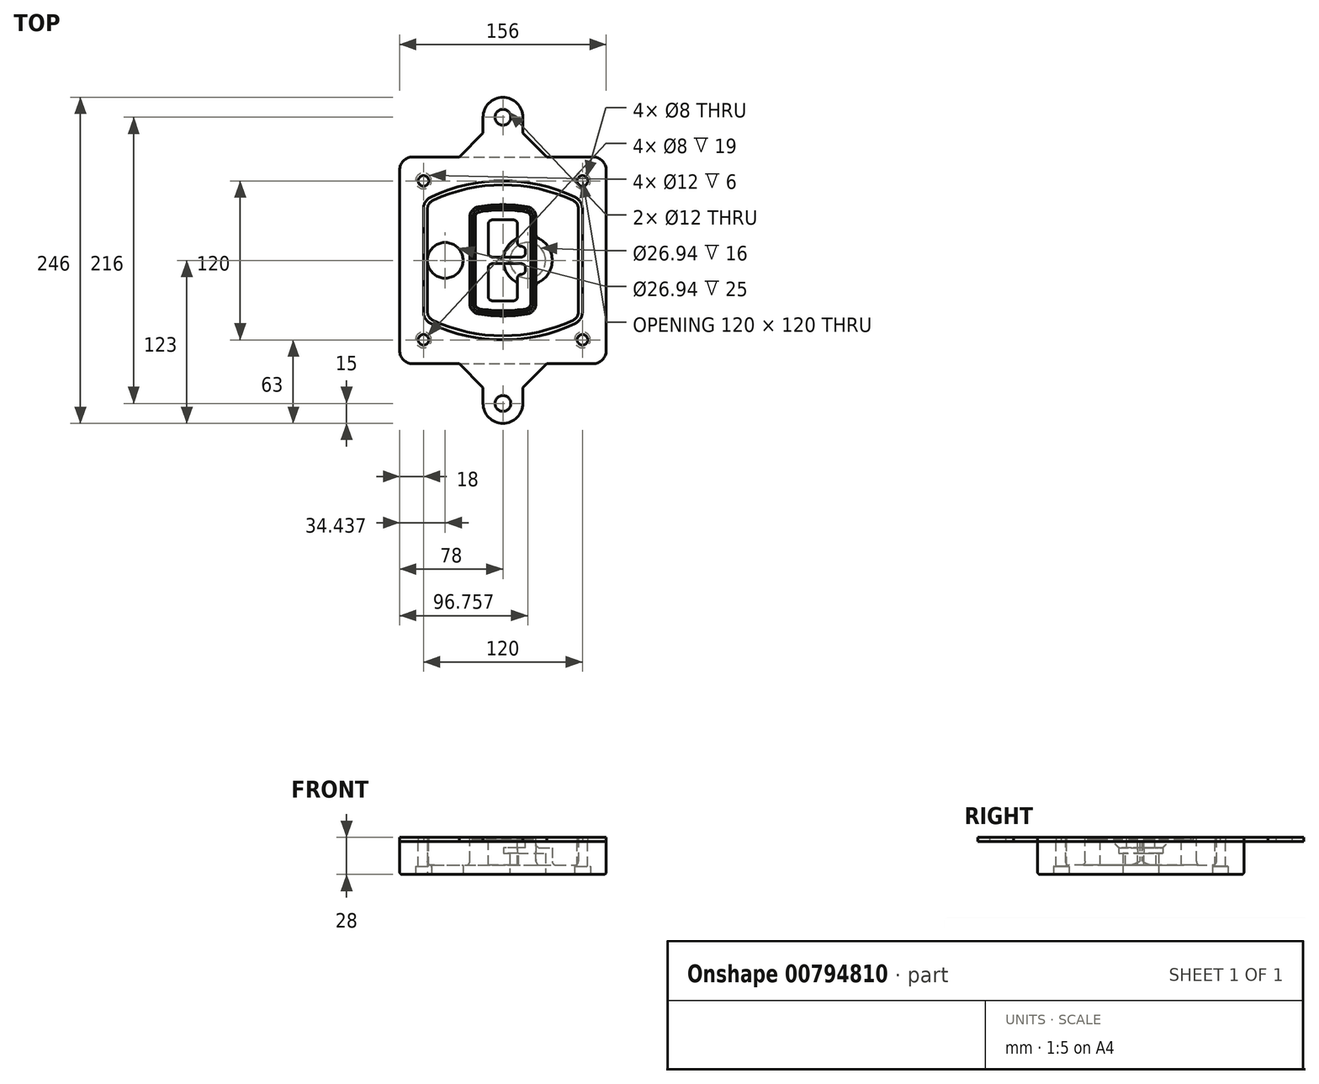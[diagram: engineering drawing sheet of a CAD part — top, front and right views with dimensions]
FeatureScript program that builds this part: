
annotation { "Feature Type Name" : "Feature", "Feature Type Description" : "" }
export const myFeature = defineFeature(function(context is Context, id is Id, definition is map)
    precondition{}
    {
        {
            var Q0;
            Q0=qCreatedBy(makeId("Top.planeOp"),FACE);
            var sketch = newSketch(context, id + "F0", { "sketchPlane" : qUnion([Q0])});
            skPoint(sketch, "E0.rect.middle", {"position": v(0, 0) * mm});
            skLineSegment(sketch, "E1.bottom", {"start": v(-68, -78) * mm, "end": v(68, -78) * mm});
            skLineSegment(sketch, "E1.top", {"start": v(-68, 78) * mm, "end": v(68, 78) * mm});
            skLineSegment(sketch, "E1.left", {"start": v(-78, -68) * mm, "end": v(-78, 68) * mm});
            skLineSegment(sketch, "E1.right", {"start": v(78, -68) * mm, "end": v(78, 68) * mm});
            skLineSegment(sketch, "E2", {"start": v(-78, 78) * mm, "end": v(78, -78) * mm, "construction": true});
            skLineSegment(sketch, "E3", {"start": v(78, 78) * mm, "end": v(-78, -78) * mm, "construction": true});
            skCircle(sketch, "E4", {"center": v(-60, 60) * mm, "radius": 4 * mm});
            skCircle(sketch, "E5", {"center": v(60, 60) * mm, "radius": 4 * mm});
            skCircle(sketch, "E6", {"center": v(60, -60) * mm, "radius": 4 * mm});
            skCircle(sketch, "E7", {"center": v(-60, -60) * mm, "radius": 4 * mm});
            skLineSegment(sketch, "E8", {"start": v(-60, 60) * mm, "end": v(60, 60) * mm, "construction": true});
            skLineSegment(sketch, "E9", {"start": v(60, 60) * mm, "end": v(60, -60) * mm, "construction": true});
            skLineSegment(sketch, "E10", {"start": v(60, -60) * mm, "end": v(-60, -60) * mm, "construction": true});
            skLineSegment(sketch, "E11", {"start": v(-60, -60) * mm, "end": v(-60, 60) * mm, "construction": true});
            skLineSegment(sketch, "E12", {"start": v(-60, 38.83) * mm, "end": v(-60, -38.83) * mm});
            skLineSegment(sketch, "E13", {"start": v(60, 38.83) * mm, "end": v(60, -38.83) * mm});
            skArc(sketch, "E14", {"start": v(54.26, 47.88) * mm, "mid": v(0, 60) * mm, "end": v(-54.26, 47.88) * mm});
            skArc(sketch, "E15", {"start": v(-54.26, -47.88) * mm, "mid": v(0, -60) * mm, "end": v(54.26, -47.88) * mm});
            skLineSegment(sketch, "E16", {"start": v(-60, 0) * mm, "end": v(60, 0) * mm, "construction": true});
            skPoint(sketch, "E17.visualSharp", {"position": v(-60, -45) * mm});
            skArc(sketch, "E17.filletArc", {"start": v(-60, -38.83) * mm, "mid": v(-58.44, -44.2) * mm, "end": v(-54.26, -47.88) * mm});
            skPoint(sketch, "E18.visualSharp", {"position": v(-60, 45) * mm});
            skArc(sketch, "E18.filletArc", {"start": v(-54.26, 47.88) * mm, "mid": v(-58.44, 44.2) * mm, "end": v(-60, 38.83) * mm});
            skPoint(sketch, "E19.visualSharp", {"position": v(60, 45) * mm});
            skArc(sketch, "E19.filletArc", {"start": v(60, 38.83) * mm, "mid": v(58.44, 44.2) * mm, "end": v(54.26, 47.88) * mm});
            skPoint(sketch, "E20.visualSharp", {"position": v(60, -45) * mm});
            skArc(sketch, "E20.filletArc", {"start": v(54.26, -47.88) * mm, "mid": v(58.44, -44.2) * mm, "end": v(60, -38.83) * mm});
            skPoint(sketch, "E21.visualSharp", {"position": v(-78, 78) * mm});
            skArc(sketch, "E21.filletArc", {"start": v(-68, 78) * mm, "mid": v(-75.07, 75.07) * mm, "end": v(-78, 68) * mm});
            skPoint(sketch, "E22.visualSharp", {"position": v(78, 78) * mm});
            skArc(sketch, "E22.filletArc", {"start": v(78, 68) * mm, "mid": v(75.07, 75.07) * mm, "end": v(68, 78) * mm});
            skPoint(sketch, "E23.visualSharp", {"position": v(78, -78) * mm});
            skArc(sketch, "E23.filletArc", {"start": v(68, -78) * mm, "mid": v(75.07, -75.07) * mm, "end": v(78, -68) * mm});
            skPoint(sketch, "E24.visualSharp", {"position": v(-78, -78) * mm});
            skArc(sketch, "E24.filletArc", {"start": v(-78, -68) * mm, "mid": v(-75.07, -75.07) * mm, "end": v(-68, -78) * mm});
            skArc(sketch, "E25.0", {"start": v(57, 38.83) * mm, "mid": v(55.9, 42.58) * mm, "end": v(52.98, 45.17) * mm});
            skLineSegment(sketch, "E25.1", {"start": v(57, 38.83) * mm, "end": v(57, -38.83) * mm});
            skArc(sketch, "E25.2", {"start": v(52.98, -45.17) * mm, "mid": v(55.9, -42.58) * mm, "end": v(57, -38.83) * mm});
            skArc(sketch, "E25.3", {"start": v(-52.98, -45.17) * mm, "mid": v(0, -57) * mm, "end": v(52.98, -45.17) * mm});
            skArc(sketch, "E25.4", {"start": v(-57, -38.83) * mm, "mid": v(-55.9, -42.58) * mm, "end": v(-52.98, -45.17) * mm});
            skArc(sketch, "E25.5", {"start": v(52.98, 45.17) * mm, "mid": v(0, 57) * mm, "end": v(-52.98, 45.17) * mm});
            skLineSegment(sketch, "E25.6", {"start": v(-57, 38.83) * mm, "end": v(-57, -38.83) * mm});
            skArc(sketch, "E25.7", {"start": v(-52.98, 45.17) * mm, "mid": v(-55.9, 42.58) * mm, "end": v(-57, 38.83) * mm});
            skArc(sketch, "E26.0", {"start": v(-55.96, 51.5) * mm, "mid": v(-61.82, 46.33) * mm, "end": v(-64, 38.83) * mm});
            skArc(sketch, "E26.1", {"start": v(55.96, 51.5) * mm, "mid": v(0, 64) * mm, "end": v(-55.96, 51.5) * mm});
            skArc(sketch, "E26.2", {"start": v(64, 38.83) * mm, "mid": v(61.82, 46.33) * mm, "end": v(55.96, 51.5) * mm});
            skLineSegment(sketch, "E26.3", {"start": v(64, 38.83) * mm, "end": v(64, -38.83) * mm});
            skArc(sketch, "E26.4", {"start": v(55.96, -51.5) * mm, "mid": v(61.82, -46.33) * mm, "end": v(64, -38.83) * mm});
            skLineSegment(sketch, "E26.5", {"start": v(-64, 38.83) * mm, "end": v(-64, -38.83) * mm});
            skArc(sketch, "E26.6", {"start": v(-55.96, -51.5) * mm, "mid": v(0, -64) * mm, "end": v(55.96, -51.5) * mm});
            skArc(sketch, "E26.7", {"start": v(-64, -38.83) * mm, "mid": v(-61.82, -46.33) * mm, "end": v(-55.96, -51.5) * mm});
            skSolve(sketch);
        }
        {
            var Q0;
            Q0=makeQuery(id+"F0.imprint","IMPRINT",FACE,{"disambiguationData":[TD([[makeQuery(id+"F0.imprint","IMPRINT",EDGE,{"derivedFrom":sQuery(id+"F0.wireOp",EDGE,"E1.bottom")}),1.0]])]});
            var Q1;
            Q1=makeQuery(id+"F0.imprint","IMPRINT",FACE,{"disambiguationData":[TD([[makeQuery(id+"F0.imprint","IMPRINT",EDGE,{"derivedFrom":sQuery(id+"F0.wireOp",EDGE,"E12")}),1.0]])]});
            var Q2;
            Q2=makeQuery(id+"F0.imprint","IMPRINT",FACE,{"disambiguationData":[TD([[makeQuery(id+"F0.imprint","IMPRINT",EDGE,{"derivedFrom":sQuery(id+"F0.wireOp",EDGE,"E25.0")}),1.0]])]});
            var Q3;
            Q3=makeQuery(id+"F0.imprint","IMPRINT",FACE,{"disambiguationData":[TD([[makeQuery(id+"F0.imprint","IMPRINT",EDGE,{"derivedFrom":sQuery(id+"F0.wireOp",EDGE,"E12")}),-1.0]])]});
            extrude(context, id + "F1", {"entities" : qUnion([Q0, Q1, Q2, Q3]), "oppositeDirection" : true, "depth" : 25 * mm});
        }
        {
            var Q0;
            Q0=makeQuery(id+"F0.imprint","IMPRINT",FACE,{"disambiguationData":[TD([[makeQuery(id+"F0.imprint","IMPRINT",EDGE,{"derivedFrom":sQuery(id+"F0.wireOp",EDGE,"E12")}),1.0]])]});
            extrude(context, id + "F2", {"entities" : qUnion([Q0]), "operationType" : NewBodyOperationType.ADD, "depth" : 3 * mm});
        }
        {
            var Q0;
            Q0=makeQuery(id+"F0.imprint","IMPRINT",FACE,{"disambiguationData":[TD([[makeQuery(id+"F0.imprint","IMPRINT",EDGE,{"derivedFrom":sQuery(id+"F0.wireOp",EDGE,"E25.0")}),1.0]])]});
            extrude(context, id + "F3", {"entities" : qUnion([Q0]), "operationType" : NewBodyOperationType.REMOVE, "oppositeDirection" : true, "depth" : 18 * mm});
        }
        {
            var Q0;
            Q0=makeQuery(id+"F2.opExtrude","CAP_FACE",FACE,{"disambiguationData":[OSD([sQuery(id+"F0.wireOp",EDGE,"E12"),sQuery(id+"F0.wireOp",EDGE,"E13"),sQuery(id+"F0.wireOp",EDGE,"E14"),sQuery(id+"F0.wireOp",EDGE,"E15"),sQuery(id+"F0.wireOp",EDGE,"E17.filletArc"),sQuery(id+"F0.wireOp",EDGE,"E18.filletArc"),sQuery(id+"F0.wireOp",EDGE,"E19.filletArc"),sQuery(id+"F0.wireOp",EDGE,"E20.filletArc"),sQuery(id+"F0.wireOp",EDGE,"E25.0"),sQuery(id+"F0.wireOp",EDGE,"E25.1"),sQuery(id+"F0.wireOp",EDGE,"E25.2"),sQuery(id+"F0.wireOp",EDGE,"E25.3"),sQuery(id+"F0.wireOp",EDGE,"E25.4"),sQuery(id+"F0.wireOp",EDGE,"E25.5"),sQuery(id+"F0.wireOp",EDGE,"E25.6"),sQuery(id+"F0.wireOp",EDGE,"E25.7")])],"isStart":false});
            var sketch = newSketch(context, id + "F4", { "sketchPlane" : qUnion([Q0])});
            skArc(sketch, "E27.0", {"start": v(-18.34, -40.45) * mm, "mid": v(0, -42) * mm, "end": v(18.34, -40.45) * mm});
            skArc(sketch, "E28.0", {"start": v(18.34, 40.45) * mm, "mid": v(0, 42) * mm, "end": v(-18.34, 40.45) * mm});
            skLineSegment(sketch, "E29", {"start": v(-25, 32.57) * mm, "end": v(-25, -32.57) * mm});
            skLineSegment(sketch, "E30", {"start": v(25, 32.57) * mm, "end": v(25, -32.57) * mm});
            skLineSegment(sketch, "E31", {"start": v(-25, 39.1) * mm, "end": v(25, 39.1) * mm, "construction": true});
            skLineSegment(sketch, "E32", {"start": v(-25, -39.1) * mm, "end": v(25, -39.1) * mm, "construction": true});
            skPoint(sketch, "E33.visualSharp", {"position": v(-25, 39.1) * mm});
            skArc(sketch, "E33.filletArc", {"start": v(-18.34, 40.45) * mm, "mid": v(-23.11, 37.73) * mm, "end": v(-25, 32.57) * mm});
            skPoint(sketch, "E34.visualSharp", {"position": v(25, 39.1) * mm});
            skArc(sketch, "E34.filletArc", {"start": v(25, 32.57) * mm, "mid": v(23.11, 37.73) * mm, "end": v(18.34, 40.45) * mm});
            skPoint(sketch, "E35.visualSharp", {"position": v(25, -39.1) * mm});
            skArc(sketch, "E35.filletArc", {"start": v(18.34, -40.45) * mm, "mid": v(23.11, -37.73) * mm, "end": v(25, -32.57) * mm});
            skPoint(sketch, "E36.visualSharp", {"position": v(-25, -39.1) * mm});
            skArc(sketch, "E36.filletArc", {"start": v(-25, -32.57) * mm, "mid": v(-23.11, -37.73) * mm, "end": v(-18.34, -40.45) * mm});
            skArc(sketch, "E37.0", {"start": v(52.98, 45.17) * mm, "mid": v(0, 57) * mm, "end": v(-52.98, 45.17) * mm});
            skArc(sketch, "E37.1", {"start": v(-52.98, 45.17) * mm, "mid": v(-55.9, 42.58) * mm, "end": v(-57, 38.83) * mm});
            skLineSegment(sketch, "E37.2", {"start": v(-57, 38.83) * mm, "end": v(-57, -38.83) * mm});
            skArc(sketch, "E37.3", {"start": v(-57, -38.83) * mm, "mid": v(-55.9, -42.58) * mm, "end": v(-52.98, -45.17) * mm});
            skArc(sketch, "E37.4", {"start": v(-52.98, -45.17) * mm, "mid": v(0, -57) * mm, "end": v(52.98, -45.17) * mm});
            skArc(sketch, "E37.5", {"start": v(52.98, -45.17) * mm, "mid": v(55.9, -42.58) * mm, "end": v(57, -38.83) * mm});
            skLineSegment(sketch, "E37.6", {"start": v(57, 38.83) * mm, "end": v(57, -38.83) * mm});
            skArc(sketch, "E37.7", {"start": v(57, 38.83) * mm, "mid": v(55.9, 42.58) * mm, "end": v(52.98, 45.17) * mm});
            skLineSegment(sketch, "E38.0", {"start": v(23, 32.57) * mm, "end": v(23, -32.57) * mm});
            skArc(sketch, "E38.1", {"start": v(18, -38.48) * mm, "mid": v(21.58, -36.44) * mm, "end": v(23, -32.57) * mm});
            skArc(sketch, "E38.2", {"start": v(-18, -38.48) * mm, "mid": v(0, -40) * mm, "end": v(18, -38.48) * mm});
            skArc(sketch, "E38.3", {"start": v(-23, -32.57) * mm, "mid": v(-21.58, -36.44) * mm, "end": v(-18, -38.48) * mm});
            skLineSegment(sketch, "E38.4", {"start": v(-23, 32.57) * mm, "end": v(-23, -32.57) * mm});
            skArc(sketch, "E38.5", {"start": v(23, 32.57) * mm, "mid": v(21.58, 36.44) * mm, "end": v(18, 38.48) * mm});
            skArc(sketch, "E38.6", {"start": v(-18, 38.48) * mm, "mid": v(-21.58, 36.44) * mm, "end": v(-23, 32.57) * mm});
            skArc(sketch, "E38.7", {"start": v(18, 38.48) * mm, "mid": v(0, 40) * mm, "end": v(-18, 38.48) * mm});
            skArc(sketch, "E39.0", {"start": v(21, 32.57) * mm, "mid": v(20.06, 35.15) * mm, "end": v(17.67, 36.5) * mm});
            skLineSegment(sketch, "E39.1", {"start": v(21, 32.57) * mm, "end": v(21, -32.57) * mm});
            skArc(sketch, "E39.2", {"start": v(17.67, -36.5) * mm, "mid": v(20.06, -35.15) * mm, "end": v(21, -32.57) * mm});
            skArc(sketch, "E39.3", {"start": v(-17.67, -36.5) * mm, "mid": v(0, -38) * mm, "end": v(17.67, -36.5) * mm});
            skArc(sketch, "E39.4", {"start": v(-21, -32.57) * mm, "mid": v(-20.06, -35.15) * mm, "end": v(-17.67, -36.5) * mm});
            skArc(sketch, "E39.5", {"start": v(17.67, 36.5) * mm, "mid": v(0, 38) * mm, "end": v(-17.67, 36.5) * mm});
            skLineSegment(sketch, "E39.6", {"start": v(-21, 32.57) * mm, "end": v(-21, -32.57) * mm});
            skArc(sketch, "E39.7", {"start": v(-17.67, 36.5) * mm, "mid": v(-20.06, 35.15) * mm, "end": v(-21, 32.57) * mm});
            skLineSegment(sketch, "E40", {"start": v(-25, 0) * mm, "end": v(25, 0) * mm, "construction": true});
            skLineSegment(sketch, "E41", {"start": v(-11, 5.5) * mm, "end": v(-11, 27.5) * mm});
            skLineSegment(sketch, "E42", {"start": v(-8, 30.5) * mm, "end": v(8, 30.5) * mm});
            skLineSegment(sketch, "E43", {"start": v(11, 27.5) * mm, "end": v(11, 13.5) * mm});
            skLineSegment(sketch, "E44", {"start": v(14, 10.5) * mm, "end": v(14, 10.5) * mm});
            skLineSegment(sketch, "E45", {"start": v(17, 7.5) * mm, "end": v(17, 5.5) * mm});
            skLineSegment(sketch, "E46", {"start": v(14, 2.5) * mm, "end": v(-8, 2.5) * mm});
            skPoint(sketch, "E47.visualSharp", {"position": v(-11, 30.5) * mm});
            skArc(sketch, "E47.filletArc", {"start": v(-8, 30.5) * mm, "mid": v(-10.12, 29.62) * mm, "end": v(-11, 27.5) * mm});
            skPoint(sketch, "E48.visualSharp", {"position": v(11, 30.5) * mm});
            skArc(sketch, "E48.filletArc", {"start": v(11, 27.5) * mm, "mid": v(10.12, 29.62) * mm, "end": v(8, 30.5) * mm});
            skPoint(sketch, "E49.visualSharp", {"position": v(11, 10.5) * mm});
            skArc(sketch, "E49.filletArc", {"start": v(11, 13.5) * mm, "mid": v(11.88, 11.38) * mm, "end": v(14, 10.5) * mm});
            skPoint(sketch, "E50.visualSharp", {"position": v(17, 10.5) * mm});
            skArc(sketch, "E50.filletArc", {"start": v(17, 7.5) * mm, "mid": v(16.12, 9.62) * mm, "end": v(14, 10.5) * mm});
            skPoint(sketch, "E51.visualSharp", {"position": v(17, 2.5) * mm});
            skArc(sketch, "E51.filletArc", {"start": v(14, 2.5) * mm, "mid": v(16.12, 3.38) * mm, "end": v(17, 5.5) * mm});
            skPoint(sketch, "E52.visualSharp", {"position": v(-11, 2.5) * mm});
            skArc(sketch, "E52.filletArc", {"start": v(-11, 5.5) * mm, "mid": v(-10.12, 3.38) * mm, "end": v(-8, 2.5) * mm});
            skLineSegment(sketch, "E53.0.MirrorCS", {"start": v(14, -2.5) * mm, "end": v(-8, -2.5) * mm});
            skArc(sketch, "E54.0.MirrorCS", {"start": v(-11, -5.5) * mm, "mid": v(-10.12, -3.38) * mm, "end": v(-8, -2.5) * mm});
            skLineSegment(sketch, "E55.0.MirrorCS", {"start": v(-11, -5.5) * mm, "end": v(-11, -27.5) * mm});
            skArc(sketch, "E56.0.MirrorCS", {"start": v(-8, -30.5) * mm, "mid": v(-10.12, -29.62) * mm, "end": v(-11, -27.5) * mm});
            skLineSegment(sketch, "E57.0.MirrorCS", {"start": v(-8, -30.5) * mm, "end": v(8, -30.5) * mm});
            skArc(sketch, "E58.0.MirrorCS", {"start": v(11, -27.5) * mm, "mid": v(10.12, -29.62) * mm, "end": v(8, -30.5) * mm});
            skLineSegment(sketch, "E59.0.MirrorCS", {"start": v(11, -27.5) * mm, "end": v(11, -13.5) * mm});
            skArc(sketch, "E60.0.MirrorCS", {"start": v(11, -13.5) * mm, "mid": v(11.88, -11.38) * mm, "end": v(14, -10.5) * mm});
            skArc(sketch, "E61.0.MirrorCS", {"start": v(17, -7.5) * mm, "mid": v(16.12, -9.62) * mm, "end": v(14, -10.5) * mm});
            skLineSegment(sketch, "E62.0.MirrorCS", {"start": v(17, -7.5) * mm, "end": v(17, -5.5) * mm});
            skArc(sketch, "E63.0.MirrorCS", {"start": v(14, -2.5) * mm, "mid": v(16.12, -3.38) * mm, "end": v(17, -5.5) * mm});
            skSolve(sketch);
        }
        {
            var Q0;
            Q0=makeQuery(id+"F4.imprint","IMPRINT",FACE,{"disambiguationData":[TD([[makeQuery(id+"F4.imprint","IMPRINT",EDGE,{"derivedFrom":sQuery(id+"F4.wireOp",EDGE,"E27.0")}),1.0]])]});
            var Q1;
            Q1=makeQuery(id+"F4.imprint","IMPRINT",FACE,{"disambiguationData":[TD([[makeQuery(id+"F4.imprint","IMPRINT",EDGE,{"derivedFrom":sQuery(id+"F4.wireOp",EDGE,"E38.0")}),-1.0]])]});
            var Q2;
            Q2=makeQuery(id+"F4.imprint","IMPRINT",FACE,{"disambiguationData":[TD([[makeQuery(id+"F4.imprint","IMPRINT",EDGE,{"derivedFrom":sQuery(id+"F4.wireOp",EDGE,"E39.0")}),1.0]])]});
            extrude(context, id + "F5", {"entities" : qUnion([Q0, Q1, Q2]), "operationType" : NewBodyOperationType.ADD, "endBound" : BoundingType.UP_TO_NEXT, "oppositeDirection" : true, "depth" : 25 * mm});
        }
        {
            var Q0;
            Q0=makeQuery(id+"F4.imprint","IMPRINT",FACE,{"disambiguationData":[TD([[makeQuery(id+"F4.imprint","IMPRINT",EDGE,{"derivedFrom":sQuery(id+"F4.wireOp",EDGE,"E38.0")}),-1.0]])]});
            extrude(context, id + "F6", {"entities" : qUnion([Q0]), "operationType" : NewBodyOperationType.REMOVE, "oppositeDirection" : true, "depth" : 2 * mm});
        }
        {
            var Q0;
            Q0=makeQuery(id+"F1.opExtrude","CAP_FACE",FACE,{"disambiguationData":[OSD([sQuery(id+"F0.wireOp",EDGE,"E1.bottom"),sQuery(id+"F0.wireOp",EDGE,"E1.top"),sQuery(id+"F0.wireOp",EDGE,"E1.left"),sQuery(id+"F0.wireOp",EDGE,"E1.right"),sQuery(id+"F0.wireOp",EDGE,"E4"),sQuery(id+"F0.wireOp",EDGE,"E5"),sQuery(id+"F0.wireOp",EDGE,"E6"),sQuery(id+"F0.wireOp",EDGE,"E7"),sQuery(id+"F0.wireOp",EDGE,"E21.filletArc"),sQuery(id+"F0.wireOp",EDGE,"E22.filletArc"),sQuery(id+"F0.wireOp",EDGE,"E23.filletArc"),sQuery(id+"F0.wireOp",EDGE,"E24.filletArc")])],"isStart":false});
            var sketch = newSketch(context, id + "F7", { "sketchPlane" : qUnion([Q0])});
            skCircle(sketch, "E64", {"center": v(18.76, 0) * mm, "radius": 13.47 * mm});
            skCircle(sketch, "E65", {"center": v(-43.56, 0) * mm, "radius": 13.47 * mm});
            skLineSegment(sketch, "E66", {"start": v(78, 0) * mm, "end": v(-78, 0) * mm});
            skCircle(sketch, "E67", {"center": v(18.76, 0) * mm, "radius": 18.47 * mm});
            skCircle(sketch, "E68", {"center": v(60, -60) * mm, "radius": 6 * mm});
            skCircle(sketch, "E69", {"center": v(-60, -60) * mm, "radius": 6 * mm});
            skCircle(sketch, "E70", {"center": v(-60, 60) * mm, "radius": 6 * mm});
            skCircle(sketch, "E71", {"center": v(60, 60) * mm, "radius": 6 * mm});
            skSolve(sketch);
        }
        {
            var Q0;
            {var subQ1=sQuery(id+"F7.wireOp",EDGE,"E66");var subQ4=sQuery(id+"F7.wireOp",EDGE,"E64");var subQ6=makeQuery(id+"F7.imprint","INTERSECT",VERTEX,{"disambiguationData":[OD(0.0)],"derivedFrom":[subQ4,subQ1]});Q0=makeQuery(id+"F7.imprint","IMPRINT",FACE,{"disambiguationData":[TD([[makeQuery(id+"F7.imprint","IMPRINT",EDGE,{"disambiguationData":[TD([[subQ6,-1.0]])],"derivedFrom":subQ4}),-1.0]])]});}
            var Q1;
            {var subQ0=sQuery(id+"F7.wireOp",EDGE,"E66");var subQ1=sQuery(id+"F7.wireOp",EDGE,"E64");var subQ3=makeQuery(id+"F7.imprint","INTERSECT",VERTEX,{"disambiguationData":[OD(0.0)],"derivedFrom":[subQ1,subQ0]});Q1=makeQuery(id+"F7.imprint","IMPRINT",FACE,{"disambiguationData":[TD([[makeQuery(id+"F7.imprint","IMPRINT",EDGE,{"disambiguationData":[TD([[subQ3,-1.0]])],"derivedFrom":subQ1}),1.0]])]});}
            var Q2;
            {var subQ0=sQuery(id+"F7.wireOp",EDGE,"E66");var subQ1=sQuery(id+"F7.wireOp",EDGE,"E64");var subQ3=makeQuery(id+"F7.imprint","INTERSECT",VERTEX,{"disambiguationData":[OD(0.0)],"derivedFrom":[subQ1,subQ0]});Q2=makeQuery(id+"F7.imprint","IMPRINT",FACE,{"disambiguationData":[TD([[makeQuery(id+"F7.imprint","IMPRINT",EDGE,{"disambiguationData":[TD([[subQ3,1.0]])],"derivedFrom":subQ1}),1.0]])]});}
            var Q3;
            {var subQ1=sQuery(id+"F7.wireOp",EDGE,"E66");var subQ4=sQuery(id+"F7.wireOp",EDGE,"E64");var subQ6=makeQuery(id+"F7.imprint","INTERSECT",VERTEX,{"disambiguationData":[OD(0.0)],"derivedFrom":[subQ4,subQ1]});Q3=makeQuery(id+"F7.imprint","IMPRINT",FACE,{"disambiguationData":[TD([[makeQuery(id+"F7.imprint","IMPRINT",EDGE,{"disambiguationData":[TD([[subQ6,1.0]])],"derivedFrom":subQ4}),-1.0]])]});}
            extrude(context, id + "F8", {"entities" : qUnion([Q0, Q1, Q2, Q3]), "operationType" : NewBodyOperationType.ADD, "oppositeDirection" : true, "depth" : 20 * mm});
        }
        {
            var Q0;
            {var subQ0=sQuery(id+"F7.wireOp",EDGE,"E66");var subQ1=sQuery(id+"F7.wireOp",EDGE,"E64");var subQ3=makeQuery(id+"F7.imprint","INTERSECT",VERTEX,{"disambiguationData":[OD(0.0)],"derivedFrom":[subQ1,subQ0]});Q0=makeQuery(id+"F7.imprint","IMPRINT",FACE,{"disambiguationData":[TD([[makeQuery(id+"F7.imprint","IMPRINT",EDGE,{"disambiguationData":[TD([[subQ3,-1.0]])],"derivedFrom":subQ1}),1.0]])]});}
            var Q1;
            {var subQ0=sQuery(id+"F7.wireOp",EDGE,"E66");var subQ1=sQuery(id+"F7.wireOp",EDGE,"E64");var subQ3=makeQuery(id+"F7.imprint","INTERSECT",VERTEX,{"disambiguationData":[OD(0.0)],"derivedFrom":[subQ1,subQ0]});Q1=makeQuery(id+"F7.imprint","IMPRINT",FACE,{"disambiguationData":[TD([[makeQuery(id+"F7.imprint","IMPRINT",EDGE,{"disambiguationData":[TD([[subQ3,1.0]])],"derivedFrom":subQ1}),1.0]])]});}
            extrude(context, id + "F9", {"entities" : qUnion([Q0, Q1]), "operationType" : NewBodyOperationType.REMOVE, "oppositeDirection" : true, "depth" : 16 * mm});
        }
        {
            var Q0;
            {var subQ0=sQuery(id+"F7.wireOp",EDGE,"E66");var subQ1=sQuery(id+"F7.wireOp",EDGE,"E65");var subQ3=makeQuery(id+"F7.imprint","INTERSECT",VERTEX,{"disambiguationData":[OD(0.0)],"derivedFrom":[subQ1,subQ0]});Q0=makeQuery(id+"F7.imprint","IMPRINT",FACE,{"disambiguationData":[TD([[makeQuery(id+"F7.imprint","IMPRINT",EDGE,{"disambiguationData":[TD([[subQ3,-1.0]])],"derivedFrom":subQ1}),1.0]])]});}
            var Q1;
            {var subQ0=sQuery(id+"F7.wireOp",EDGE,"E66");var subQ1=sQuery(id+"F7.wireOp",EDGE,"E65");var subQ3=makeQuery(id+"F7.imprint","INTERSECT",VERTEX,{"disambiguationData":[OD(0.0)],"derivedFrom":[subQ1,subQ0]});Q1=makeQuery(id+"F7.imprint","IMPRINT",FACE,{"disambiguationData":[TD([[makeQuery(id+"F7.imprint","IMPRINT",EDGE,{"disambiguationData":[TD([[subQ3,1.0]])],"derivedFrom":subQ1}),1.0]])]});}
            extrude(context, id + "F10", {"entities" : qUnion([Q0, Q1]), "operationType" : NewBodyOperationType.REMOVE, "oppositeDirection" : true, "depth" : 25 * mm});
        }
        {
            var Q0;
            Q0=makeQuery(id+"F7.imprint","IMPRINT",FACE,{"disambiguationData":[TD([[makeQuery(id+"F7.imprint","IMPRINT",EDGE,{"derivedFrom":sQuery(id+"F7.wireOp",EDGE,"E68")}),1.0]])]});
            var Q1;
            Q1=makeQuery(id+"F7.imprint","IMPRINT",FACE,{"disambiguationData":[TD([[makeQuery(id+"F7.imprint","IMPRINT",EDGE,{"derivedFrom":makeQuery(id+"F1.opExtrude","CAP_EDGE",EDGE,{"disambiguationData":[OSD([sQuery(id+"F0.wireOp",EDGE,"E5")])],"isStart":false})}),-1.0]])]});
            var Q2;
            Q2=makeQuery(id+"F7.imprint","IMPRINT",FACE,{"disambiguationData":[TD([[makeQuery(id+"F7.imprint","IMPRINT",EDGE,{"derivedFrom":sQuery(id+"F7.wireOp",EDGE,"E69")}),1.0]])]});
            var Q3;
            Q3=makeQuery(id+"F7.imprint","IMPRINT",FACE,{"disambiguationData":[TD([[makeQuery(id+"F7.imprint","IMPRINT",EDGE,{"derivedFrom":makeQuery(id+"F1.opExtrude","CAP_EDGE",EDGE,{"disambiguationData":[OSD([sQuery(id+"F0.wireOp",EDGE,"E4")])],"isStart":false})}),-1.0]])]});
            var Q4;
            Q4=makeQuery(id+"F7.imprint","IMPRINT",FACE,{"disambiguationData":[TD([[makeQuery(id+"F7.imprint","IMPRINT",EDGE,{"derivedFrom":sQuery(id+"F7.wireOp",EDGE,"E70")}),1.0]])]});
            var Q5;
            Q5=makeQuery(id+"F7.imprint","IMPRINT",FACE,{"disambiguationData":[TD([[makeQuery(id+"F7.imprint","IMPRINT",EDGE,{"derivedFrom":makeQuery(id+"F1.opExtrude","CAP_EDGE",EDGE,{"disambiguationData":[OSD([sQuery(id+"F0.wireOp",EDGE,"E7")])],"isStart":false})}),-1.0]])]});
            var Q6;
            Q6=makeQuery(id+"F7.imprint","IMPRINT",FACE,{"disambiguationData":[TD([[makeQuery(id+"F7.imprint","IMPRINT",EDGE,{"derivedFrom":sQuery(id+"F7.wireOp",EDGE,"E71")}),1.0]])]});
            var Q7;
            Q7=makeQuery(id+"F7.imprint","IMPRINT",FACE,{"disambiguationData":[TD([[makeQuery(id+"F7.imprint","IMPRINT",EDGE,{"derivedFrom":makeQuery(id+"F1.opExtrude","CAP_EDGE",EDGE,{"disambiguationData":[OSD([sQuery(id+"F0.wireOp",EDGE,"E6")])],"isStart":false})}),-1.0]])]});
            extrude(context, id + "F11", {"entities" : qUnion([Q0, Q1, Q2, Q3, Q4, Q5, Q6, Q7]), "operationType" : NewBodyOperationType.REMOVE, "oppositeDirection" : true, "depth" : 6 * mm});
        }
        {
            var Q0;
            Q0=makeQuery(id+"F9.boolean.opBoolean","COPY",FACE,{"derivedFrom":makeQuery(id+"F9.opExtrude","CAP_FACE",FACE,{"disambiguationData":[OSD([sQuery(id+"F7.wireOp",EDGE,"E64")])],"isStart":false})});
            var sketch = newSketch(context, id + "F12", { "sketchPlane" : qUnion([Q0])});
            skArc(sketch, "E72.0", {"start": v(11, 16.76) * mm, "mid": v(3.9, 10.98) * mm, "end": v(0.46, 2.5) * mm});
            skArc(sketch, "E72.1", {"start": v(0.46, -2.5) * mm, "mid": v(3.9, -10.98) * mm, "end": v(11, -16.76) * mm});
            skLineSegment(sketch, "E73", {"start": v(0.46, -2.5) * mm, "end": v(14, -2.5) * mm});
            skLineSegment(sketch, "E74.0", {"start": v(14, 2.5) * mm, "end": v(0.46, 2.5) * mm});
            skArc(sketch, "E74.1", {"start": v(14, 2.5) * mm, "mid": v(16.12, 3.38) * mm, "end": v(17, 5.5) * mm});
            skLineSegment(sketch, "E74.2", {"start": v(17, 7.5) * mm, "end": v(17, 5.5) * mm});
            skArc(sketch, "E74.3", {"start": v(17, 7.5) * mm, "mid": v(16.12, 9.62) * mm, "end": v(14, 10.5) * mm});
            skArc(sketch, "E74.4", {"start": v(11, 13.5) * mm, "mid": v(11.88, 11.38) * mm, "end": v(14, 10.5) * mm});
            skLineSegment(sketch, "E74.5", {"start": v(11, 16.76) * mm, "end": v(11, 13.5) * mm});
            skLineSegment(sketch, "E74.7", {"start": v(14, -2.5) * mm, "end": v(0.46, -2.5) * mm});
            skArc(sketch, "E74.8", {"start": v(14, -2.5) * mm, "mid": v(16.12, -3.38) * mm, "end": v(17, -5.5) * mm});
            skLineSegment(sketch, "E74.9", {"start": v(17, -7.5) * mm, "end": v(17, -5.5) * mm});
            skArc(sketch, "E74.10", {"start": v(17, -7.5) * mm, "mid": v(16.12, -9.62) * mm, "end": v(14, -10.5) * mm});
            skArc(sketch, "E74.11", {"start": v(11, -13.5) * mm, "mid": v(11.88, -11.38) * mm, "end": v(14, -10.5) * mm});
            skLineSegment(sketch, "E74.12", {"start": v(11, -16.76) * mm, "end": v(11, -13.5) * mm});
            skPoint(sketch, "E75.orphan", {"position": v(11, -27.5) * mm});
            skPoint(sketch, "E76.orphan", {"position": v(-8, -2.5) * mm});
            skPoint(sketch, "E77.orphan", {"position": v(-8, 2.5) * mm});
            skPoint(sketch, "E78.orphan", {"position": v(11, 27.5) * mm});
            skSolve(sketch);
        }
        {
            var Q0;
            {var subQ7=sQuery(id+"F12.wireOp",EDGE,"E72.0");var subQ14=sQuery(id+"F12.wireOp",EDGE,"E72.1");var subQ16=sQuery(id+"F12.wireOp",EDGE,"E74.1");var subQ18=sQuery(id+"F12.wireOp",EDGE,"E74.8");Q0=qUnion([makeQuery(id+"F12.imprint","IMPRINT",FACE,{"disambiguationData":[TD([[makeQuery(id+"F12.imprint","IMPRINT",EDGE,{"derivedFrom":subQ7}),1.0]])]}),makeQuery(id+"F12.imprint","IMPRINT",FACE,{"disambiguationData":[TD([[makeQuery(id+"F12.imprint","IMPRINT",EDGE,{"derivedFrom":subQ14}),1.0]])]}),makeQuery(id+"F12.imprint","IMPRINT",FACE,{"disambiguationData":[TD([[makeQuery(id+"F12.imprint","IMPRINT",EDGE,{"derivedFrom":subQ16}),1.0]])]}),makeQuery(id+"F12.imprint","IMPRINT",FACE,{"disambiguationData":[TD([[makeQuery(id+"F12.imprint","IMPRINT",EDGE,{"derivedFrom":subQ18}),-1.0]])]})]);}
            var Q1;
            Q1=makeQuery(id+"F5.boolean.opBoolean","SPLIT",FACE,{"disambiguationData":[TD([makeQuery(id+"F5.opExtrude","SWEPT_FACE",FACE,{"disambiguationData":[OSD([sQuery(id+"F4.wireOp",EDGE,"E41")])]})])],"derivedFrom":makeQuery(id+"F3.boolean.opBoolean","COPY",FACE,{"derivedFrom":makeQuery(id+"F3.opExtrude","CAP_FACE",FACE,{"disambiguationData":[OSD([sQuery(id+"F0.wireOp",EDGE,"E25.0"),sQuery(id+"F0.wireOp",EDGE,"E25.1"),sQuery(id+"F0.wireOp",EDGE,"E25.2"),sQuery(id+"F0.wireOp",EDGE,"E25.3"),sQuery(id+"F0.wireOp",EDGE,"E25.4"),sQuery(id+"F0.wireOp",EDGE,"E25.5"),sQuery(id+"F0.wireOp",EDGE,"E25.6"),sQuery(id+"F0.wireOp",EDGE,"E25.7")])],"isStart":false})})});
            extrude(context, id + "F13", {"entities" : qUnion([Q0]), "operationType" : NewBodyOperationType.REMOVE, "endBound" : BoundingType.UP_TO_SURFACE, "endBoundEntityFace" : qUnion([Q1]), "depth" : 25 * mm});
        }
        {
            var Q0;
            Q0=makeQuery(id+"F3.boolean.opBoolean","COPY",EDGE,{"derivedFrom":makeQuery(id+"F3.opExtrude","CAP_EDGE",EDGE,{"disambiguationData":[OSD([sQuery(id+"F0.wireOp",EDGE,"E25.6")])],"isStart":false})});
            var Q1;
            Q1=makeQuery(id+"F8.boolean.opBoolean","INTERSECT",EDGE,{"derivedFrom":[makeQuery(id+"F5.opExtrude","SWEPT_FACE",FACE,{"disambiguationData":[OSD([sQuery(id+"F4.wireOp",EDGE,"E30")])]}),makeQuery(id+"F8.opExtrude","CAP_FACE",FACE,{"disambiguationData":[OSD([sQuery(id+"F7.wireOp",EDGE,"E67")])],"isStart":false})]});
            var Q2;
            Q2=makeQuery(id+"F8.boolean.opBoolean","INTERSECT",EDGE,{"disambiguationData":[OD(1.0)],"derivedFrom":[makeQuery(id+"F5.opExtrude","SWEPT_FACE",FACE,{"disambiguationData":[OSD([sQuery(id+"F4.wireOp",EDGE,"E30")])]}),makeQuery(id+"F8.opExtrude","SWEPT_FACE",FACE,{"disambiguationData":[OSD([sQuery(id+"F7.wireOp",EDGE,"E67")])]})]});
            var Q3;
            {var subQ0=sQuery(id+"F4.wireOp",EDGE,"E30");Q3=makeQuery(id+"F8.boolean.opBoolean","SPLIT",EDGE,{"disambiguationData":[TD([makeQuery(id+"F5.opExtrude","SWEPT_FACE",FACE,{"disambiguationData":[OSD([sQuery(id+"F4.wireOp",EDGE,"E35.filletArc")])]})])],"derivedFrom":makeQuery(id+"F5.opExtrude","CAP_EDGE",EDGE,{"disambiguationData":[OSD([subQ0])],"isStart":false})});}
            var Q4;
            {var subQ0=sQuery(id+"F0.wireOp",EDGE,"E25.7");var subQ1=sQuery(id+"F0.wireOp",EDGE,"E25.1");var subQ2=sQuery(id+"F0.wireOp",EDGE,"E25.6");var subQ3=sQuery(id+"F0.wireOp",EDGE,"E25.5");var subQ4=sQuery(id+"F0.wireOp",EDGE,"E25.4");var subQ5=sQuery(id+"F0.wireOp",EDGE,"E25.0");var subQ6=sQuery(id+"F0.wireOp",EDGE,"E25.2");var subQ7=sQuery(id+"F0.wireOp",EDGE,"E25.3");Q4=makeQuery(id+"F8.boolean.opBoolean","INTERSECT",EDGE,{"derivedFrom":[makeQuery(id+"F5.boolean.opBoolean","SPLIT",FACE,{"disambiguationData":[TD([makeQuery(id+"F2.opExtrude","SWEPT_FACE",FACE,{"disambiguationData":[OSD([subQ5])]})])],"derivedFrom":makeQuery(id+"F3.boolean.opBoolean","COPY",FACE,{"derivedFrom":makeQuery(id+"F3.opExtrude","CAP_FACE",FACE,{"disambiguationData":[OSD([subQ5,subQ1,subQ6,subQ7,subQ4,subQ3,subQ2,subQ0])],"isStart":false})})}),makeQuery(id+"F8.opExtrude","SWEPT_FACE",FACE,{"disambiguationData":[OSD([sQuery(id+"F7.wireOp",EDGE,"E67")])]})]});}
            var Q5;
            Q5=makeQuery(id+"F8.boolean.opBoolean","INTERSECT",EDGE,{"disambiguationData":[OD(0.0)],"derivedFrom":[makeQuery(id+"F5.opExtrude","SWEPT_FACE",FACE,{"disambiguationData":[OSD([sQuery(id+"F4.wireOp",EDGE,"E30")])]}),makeQuery(id+"F8.opExtrude","SWEPT_FACE",FACE,{"disambiguationData":[OSD([sQuery(id+"F7.wireOp",EDGE,"E67")])]})]});
            fillet(context, id + "F14", {"entities" : qUnion([Q0, Q1, Q2, Q3, Q4, Q5]), "radius" : 3 * mm, "tangentPropagation" : true, "allowEdgeOverflow" : false});
        }
        {
            var Q0;
            Q0=makeQuery(id+"F1.opExtrude","CAP_EDGE",EDGE,{"disambiguationData":[OSD([sQuery(id+"F0.wireOp",EDGE,"E1.bottom")])],"isStart":false});
            fillet(context, id + "F15", {"entities" : qUnion([Q0]), "radius" : 2 * mm, "tangentPropagation" : true, "allowEdgeOverflow" : false});
        }
        {
            var Q0;
            {var subQ0=sQuery(id+"F0.wireOp",EDGE,"E21.filletArc");var subQ1=sQuery(id+"F0.wireOp",EDGE,"E7");var subQ2=sQuery(id+"F0.wireOp",EDGE,"E6");var subQ3=sQuery(id+"F0.wireOp",EDGE,"E5");var subQ4=sQuery(id+"F0.wireOp",EDGE,"E4");var subQ5=sQuery(id+"F0.wireOp",EDGE,"E22.filletArc");var subQ6=sQuery(id+"F0.wireOp",EDGE,"E1.bottom");var subQ7=sQuery(id+"F0.wireOp",EDGE,"E1.right");var subQ8=sQuery(id+"F0.wireOp",EDGE,"E1.top");var subQ9=sQuery(id+"F0.wireOp",EDGE,"E1.left");var subQ10=sQuery(id+"F0.wireOp",EDGE,"E23.filletArc");var subQ11=sQuery(id+"F0.wireOp",EDGE,"E24.filletArc");Q0=makeQuery(id+"F2.boolean.opBoolean","SPLIT",FACE,{"disambiguationData":[TD([makeQuery(id+"F1.opExtrude","SWEPT_FACE",FACE,{"disambiguationData":[OSD([subQ6])]})])],"derivedFrom":makeQuery(id+"F1.opExtrude","CAP_FACE",FACE,{"disambiguationData":[OSD([subQ6,subQ8,subQ9,subQ7,subQ4,subQ3,subQ2,subQ1,subQ0,subQ5,subQ10,subQ11])],"isStart":true})});}
            var sketch = newSketch(context, id + "F16", { "sketchPlane" : qUnion([Q0])});
            skLineSegment(sketch, "E79.0", {"start": v(-78, -68) * mm, "end": v(-78, 68) * mm});
            skArc(sketch, "E79.1", {"start": v(-68, 78) * mm, "mid": v(-75.07, 75.07) * mm, "end": v(-78, 68) * mm});
            skLineSegment(sketch, "E79.2", {"start": v(-68, 78) * mm, "end": v(68, 78) * mm});
            skArc(sketch, "E79.3", {"start": v(78, 68) * mm, "mid": v(75.07, 75.07) * mm, "end": v(68, 78) * mm});
            skLineSegment(sketch, "E79.4", {"start": v(78, -68) * mm, "end": v(78, 68) * mm});
            skArc(sketch, "E79.5", {"start": v(68, -78) * mm, "mid": v(75.07, -75.07) * mm, "end": v(78, -68) * mm});
            skLineSegment(sketch, "E79.6", {"start": v(-68, -78) * mm, "end": v(68, -78) * mm});
            skArc(sketch, "E79.7", {"start": v(-78, -68) * mm, "mid": v(-75.07, -75.07) * mm, "end": v(-68, -78) * mm});
            skCircle(sketch, "E79.8", {"center": v(-60, -60) * mm, "radius": 4 * mm});
            skCircle(sketch, "E79.9", {"center": v(60, -60) * mm, "radius": 4 * mm});
            skCircle(sketch, "E79.10", {"center": v(60, 60) * mm, "radius": 4 * mm});
            skCircle(sketch, "E79.11", {"center": v(-60, 60) * mm, "radius": 4 * mm});
            skArc(sketch, "E79.12", {"start": v(-54.26, -47.88) * mm, "mid": v(0, -60) * mm, "end": v(54.26, -47.88) * mm});
            skLineSegment(sketch, "E79.13", {"start": v(60, 38.83) * mm, "end": v(60, -38.83) * mm});
            skArc(sketch, "E79.14", {"start": v(54.26, 47.88) * mm, "mid": v(0, 60) * mm, "end": v(-54.26, 47.88) * mm});
            skLineSegment(sketch, "E79.15", {"start": v(-60, 38.83) * mm, "end": v(-60, -38.83) * mm});
            skArc(sketch, "E79.16", {"start": v(-54.26, 47.88) * mm, "mid": v(-58.44, 44.2) * mm, "end": v(-60, 38.83) * mm});
            skArc(sketch, "E79.17", {"start": v(-60, -38.83) * mm, "mid": v(-58.44, -44.2) * mm, "end": v(-54.26, -47.88) * mm});
            skArc(sketch, "E79.18", {"start": v(60, 38.83) * mm, "mid": v(58.44, 44.2) * mm, "end": v(54.26, 47.88) * mm});
            skArc(sketch, "E79.19", {"start": v(54.26, -47.88) * mm, "mid": v(58.44, -44.2) * mm, "end": v(60, -38.83) * mm});
            skLineSegment(sketch, "E80", {"start": v(0, 78) * mm, "end": v(0, 108) * mm, "construction": true});
            skLineSegment(sketch, "E81", {"start": v(-15, 108) * mm, "end": v(-15, 96) * mm});
            skLineSegment(sketch, "E82", {"start": v(15, 96) * mm, "end": v(15, 108) * mm});
            skArc(sketch, "E83", {"start": v(15, 108) * mm, "mid": v(0, 123) * mm, "end": v(-15, 108) * mm});
            skLineSegment(sketch, "E84", {"start": v(-33, 78) * mm, "end": v(-15, 96) * mm});
            skLineSegment(sketch, "E85", {"start": v(33, 78) * mm, "end": v(15, 96) * mm});
            skCircle(sketch, "E86", {"center": v(0, 108) * mm, "radius": 6 * mm});
            skLineSegment(sketch, "E87", {"start": v(-78, 0) * mm, "end": v(78, 0) * mm, "construction": true});
            skArc(sketch, "E88.MirrorCS", {"start": v(-54.26, -47.88) * mm, "mid": v(-58.44, -44.2) * mm, "end": v(-60, -38.83) * mm});
            skLineSegment(sketch, "E89.MirrorCS", {"start": v(0, -78) * mm, "end": v(0, -108) * mm, "construction": true});
            skArc(sketch, "E90.MirrorCS", {"start": v(-68, -78) * mm, "mid": v(-75.07, -75.07) * mm, "end": v(-78, -68) * mm});
            skLineSegment(sketch, "E91.MirrorCS", {"start": v(-33, -78) * mm, "end": v(-15, -96) * mm});
            skCircle(sketch, "E92.MirrorC", {"center": v(0, -108) * mm, "radius": 6 * mm});
            skLineSegment(sketch, "E93.MirrorCS", {"start": v(-15, -108) * mm, "end": v(-15, -96) * mm});
            skArc(sketch, "E94.MirrorCS", {"start": v(54.26, -47.88) * mm, "mid": v(0, -60) * mm, "end": v(-54.26, -47.88) * mm});
            skArc(sketch, "E95.MirrorCS", {"start": v(78, -68) * mm, "mid": v(75.07, -75.07) * mm, "end": v(68, -78) * mm});
            skLineSegment(sketch, "E96.MirrorCS", {"start": v(15, -96) * mm, "end": v(15, -108) * mm});
            skLineSegment(sketch, "E97.MirrorCS", {"start": v(33, -78) * mm, "end": v(15, -96) * mm});
            skArc(sketch, "E98.MirrorCS", {"start": v(15, -108) * mm, "mid": v(0, -123) * mm, "end": v(-15, -108) * mm});
            skSolve(sketch);
        }
        {
            var Q0;
            Q0=makeQuery(id+"F16.imprint","IMPRINT",FACE,{"disambiguationData":[TD([[makeQuery(id+"F16.imprint","IMPRINT",EDGE,{"derivedFrom":sQuery(id+"F16.wireOp",EDGE,"E81")}),1.0]])]});
            var Q1;
            Q1=makeQuery(id+"F16.imprint","IMPRINT",FACE,{"disambiguationData":[TD([[makeQuery(id+"F16.imprint","IMPRINT",EDGE,{"derivedFrom":sQuery(id+"F16.wireOp",EDGE,"E79.0")}),-1.0]])]});
            var Q2;
            {var subQ0=sQuery(id+"F16.wireOp",EDGE,"E91.MirrorCS");Q2=makeQuery(id+"F16.imprint","IMPRINT",FACE,{"disambiguationData":[TD([[makeQuery(id+"F16.imprint","IMPRINT",EDGE,{"derivedFrom":subQ0}),1.0]])]});}
            var Q3;
            Q3=makeQuery(id+"F2.opExtrude","CAP_FACE",FACE,{"disambiguationData":[OSD([sQuery(id+"F0.wireOp",EDGE,"E12"),sQuery(id+"F0.wireOp",EDGE,"E13"),sQuery(id+"F0.wireOp",EDGE,"E14"),sQuery(id+"F0.wireOp",EDGE,"E15"),sQuery(id+"F0.wireOp",EDGE,"E17.filletArc"),sQuery(id+"F0.wireOp",EDGE,"E18.filletArc"),sQuery(id+"F0.wireOp",EDGE,"E19.filletArc"),sQuery(id+"F0.wireOp",EDGE,"E20.filletArc"),sQuery(id+"F0.wireOp",EDGE,"E25.0"),sQuery(id+"F0.wireOp",EDGE,"E25.1"),sQuery(id+"F0.wireOp",EDGE,"E25.2"),sQuery(id+"F0.wireOp",EDGE,"E25.3"),sQuery(id+"F0.wireOp",EDGE,"E25.4"),sQuery(id+"F0.wireOp",EDGE,"E25.5"),sQuery(id+"F0.wireOp",EDGE,"E25.6"),sQuery(id+"F0.wireOp",EDGE,"E25.7")])],"isStart":false});
            extrude(context, id + "F17", {"entities" : qUnion([Q0, Q1, Q2]), "endBound" : BoundingType.UP_TO_SURFACE, "depth" : 25 * mm, "endBoundEntityFace" : qUnion([Q3]), "offsetDistance" : 25 * mm});
        }
    });
